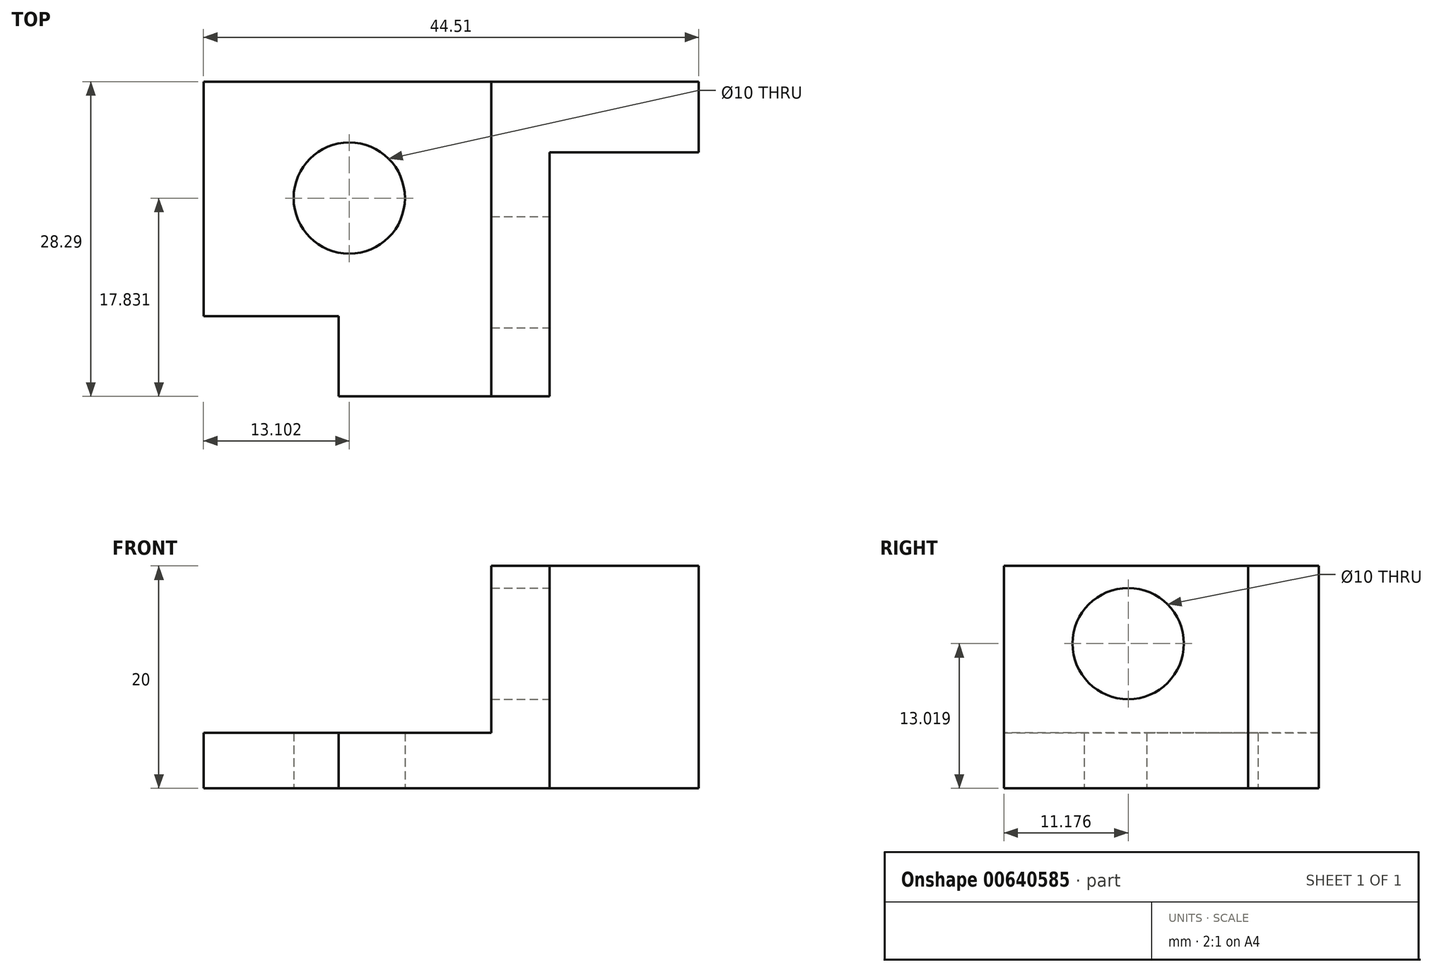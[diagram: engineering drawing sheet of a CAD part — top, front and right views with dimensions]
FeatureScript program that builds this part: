
annotation { "Feature Type Name" : "Feature", "Feature Type Description" : "" }
export const myFeature = defineFeature(function(context is Context, id is Id, definition is map)
    precondition{}
    {
        {
            var Q0;
            Q0=qCreatedBy(makeId("Top.planeOp"),FACE);
            var sketch = newSketch(context, id + "F0", { "sketchPlane" : qUnion([Q0])});
            skLineSegment(sketch, "E0", {"start": v(-31.1, 0) * mm, "end": v(-18.98, 0) * mm});
            skLineSegment(sketch, "E1", {"start": v(-18.98, 0) * mm, "end": v(-18.98, -7.22) * mm});
            skLineSegment(sketch, "E2", {"start": v(-18.98, -7.22) * mm, "end": v(0, -7.22) * mm});
            skLineSegment(sketch, "E3", {"start": v(0, -7.22) * mm, "end": v(0, 14.73) * mm});
            skLineSegment(sketch, "E4", {"start": v(0, 14.73) * mm, "end": v(13.4, 14.73) * mm});
            skLineSegment(sketch, "E5", {"start": v(13.4, 14.73) * mm, "end": v(13.4, 21.07) * mm});
            skLineSegment(sketch, "E6", {"start": v(13.4, 21.07) * mm, "end": v(-31.1, 21.07) * mm});
            skLineSegment(sketch, "E7", {"start": v(-31.1, 21.07) * mm, "end": v(-31.1, 0) * mm});
            skCircle(sketch, "E8", {"center": v(-18, 10.61) * mm, "radius": 5 * mm});
            skLineSegment(sketch, "E9", {"start": v(-5.25, -7.22) * mm, "end": v(-5.25, 21.07) * mm});
            skSolve(sketch);
        }
        {
            var Q0;
            Q0=makeQuery(id+"F0.imprint","IMPRINT",FACE,{"disambiguationData":[TD([[makeQuery(id+"F0.imprint","IMPRINT",EDGE,{"derivedFrom":sQuery(id+"F0.wireOp",EDGE,"E0")}),1.0]])]});
            extrude(context, id + "F1", {"entities" : qUnion([Q0]), "depth" : 5 * mm, "offsetDistance" : 25 * mm});
        }
        {
            var Q0;
            {var subQ1=sQuery(id+"F0.wireOp",EDGE,"E3");Q0=makeQuery(id+"F0.imprint","IMPRINT",FACE,{"disambiguationData":[TD([[makeQuery(id+"F0.imprint","IMPRINT",EDGE,{"derivedFrom":subQ1}),1.0]])]});}
            extrude(context, id + "F2", {"entities" : qUnion([Q0]), "operationType" : NewBodyOperationType.ADD, "depth" : 20 * mm, "offsetDistance" : 25 * mm});
        }
        {
            var Q0;
            Q0=qCreatedBy(makeId("Right.planeOp"),FACE);
            var sketch = newSketch(context, id + "F3", { "sketchPlane" : qUnion([Q0])});
            skCircle(sketch, "E10", {"center": v(3.96, 13.02) * mm, "radius": 5 * mm});
            skSolve(sketch);
        }
        {
            var Q0;
            Q0=makeQuery(id+"F3.imprint","IMPRINT",FACE,{"disambiguationData":[TD([[makeQuery(id+"F3.imprint","IMPRINT",EDGE,{"derivedFrom":sQuery(id+"F3.wireOp",EDGE,"E10")}),1.0]])]});
            extrude(context, id + "F4", {"entities" : qUnion([Q0]), "operationType" : NewBodyOperationType.REMOVE, "oppositeDirection" : true, "depth" : 25 * mm, "offsetDistance" : 25 * mm});
        }
    });
